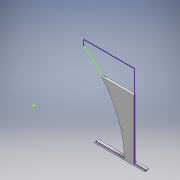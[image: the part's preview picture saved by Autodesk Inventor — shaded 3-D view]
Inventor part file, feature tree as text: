
AUTODESK INVENTOR PART (.ipt)
format: ipt  version: 2018 (Build 220112000, 112)  size: 1,147,392 bytes
history: native  units: mm
features: sketch x14, extrude x9, emboss x2
ambient origin geometry x8: Origin, YZ Plane, XZ Plane, XY Plane, X Axis, Y Axis, Z Axis, Center Point
bodies: Solid1 (feature_tree)
feature tree (25):
  extrude  "Extrusion1"  Depth=450.0mm
  extrude  "Extrusion2"  Depth=3.0mm
  extrude  "Extrusion3"  Depth=3.0mm
  extrude  "Extrusion4"  Depth=3.0mm TaperAngle=0.0deg
  extrude  "Extrusion5"  Depth=3.0mm
  extrude  "Extrusion6"  Depth=25.0mm TaperAngle=0.0deg
  emboss  "Emboss1"
  sketch  "Sketch8"  dims[d20=2.0mm d21=0.0mm d22=2.0mm d23=0.0mm]
  sketch  "Sketch9"  dims[d24=7.0mm d26=2.0mm d27=0.0mm]
  extrude  "Extrusion7"  Depth=2.0mm
  emboss  "Emboss2"
  extrude  "Extrusion8"  Depth=2.0mm TaperAngle=0.0deg
  extrude  "Extrusion9"  Depth=2.0mm TaperAngle=0.0deg
  sketch  "Sketch14"
  sketch  "Sketch1"  dims[d0=450.0mm d1=450.0mm]
  sketch  "Sketch2"  dims[d2=3.0mm d3=0.0mm d4=410.0mm]
  sketch  "Sketch3"  dims[d5=3.0mm d6=0.0mm d7=112.5mm]
  sketch  "Sketch4"  dims[d8=3.0mm d9=0.0mm d10=3.0mm d11=0.0mm]
  sketch  "Sketch5"  dims[d12=85.0mm d13=3.0mm]
  sketch  "Sketch6"  dims[d14=6.0mm d15=0.0mm d16=25.0mm d17=0.0mm]
  sketch  "Sketch7"  dims[d18=2.0mm d19=2.0mm]
  sketch  "Sketch10"  dims[d28=2.0mm d29=0.0mm]
  sketch  "Sketch11"  dims[d30=50.0mm]
  sketch  "Sketch12"  dims[d31=5.0mm d32=0.0mm]
  sketch  "Sketch13"
